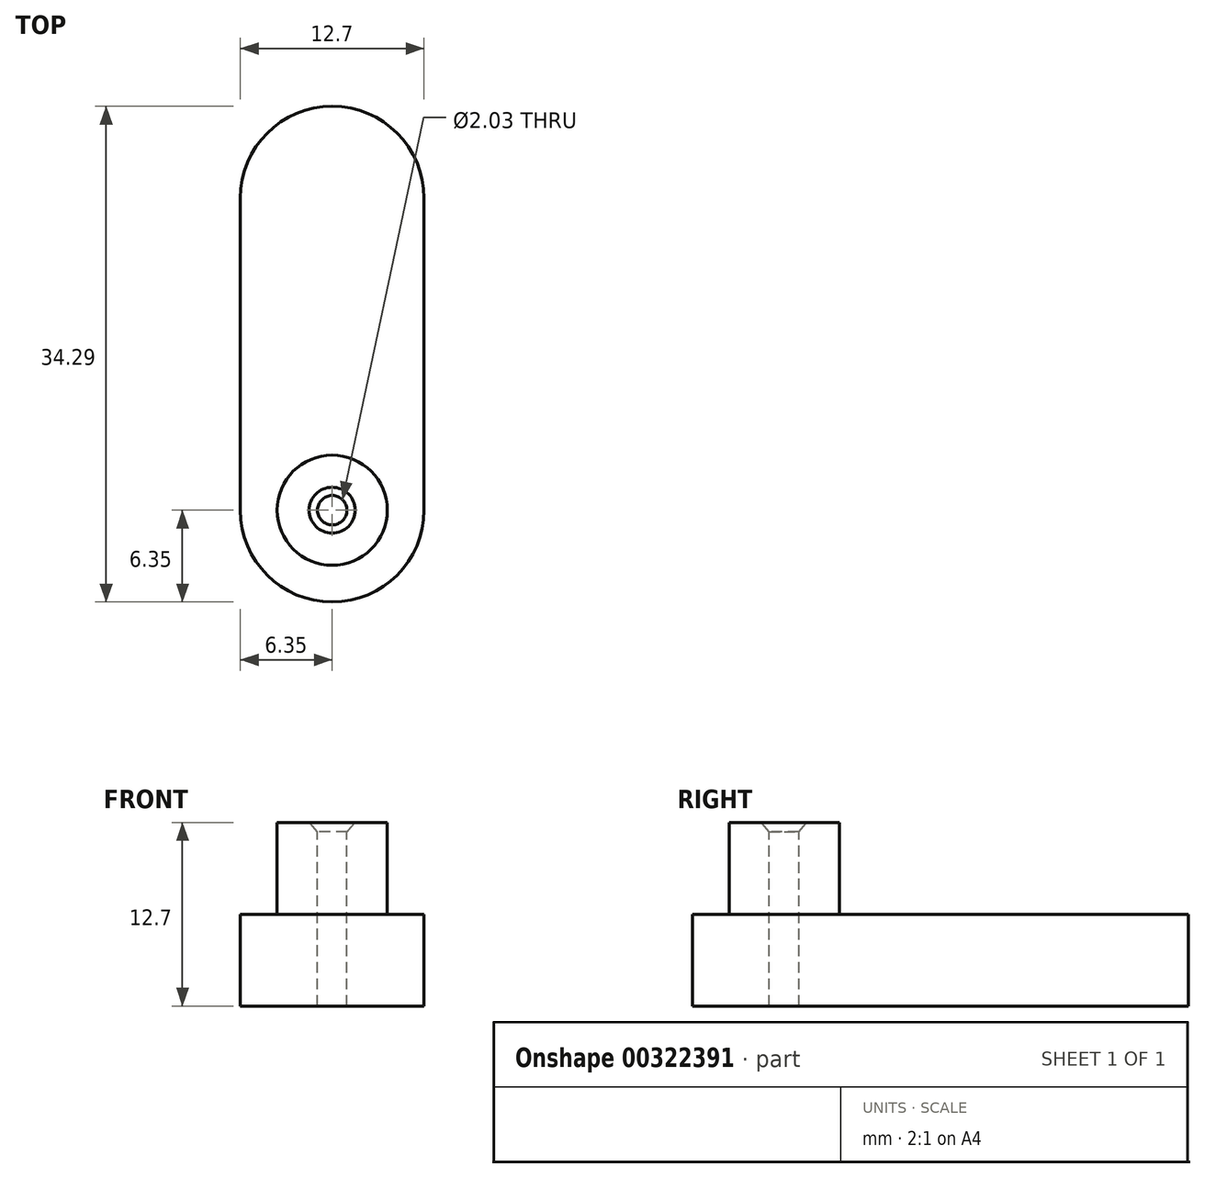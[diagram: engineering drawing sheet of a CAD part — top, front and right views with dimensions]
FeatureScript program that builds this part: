
annotation { "Feature Type Name" : "Feature", "Feature Type Description" : "" }
export const myFeature = defineFeature(function(context is Context, id is Id, definition is map)
    precondition{}
    {
        {
            var Q0;
            Q0=qCreatedBy(makeId("Top.planeOp"),FACE);
            var sketch = newSketch(context, id + "F0", { "sketchPlane" : qUnion([Q0])});
            skLineSegment(sketch, "E0", {"start": v(0, 0) * mm, "end": v(0, 12.7) * mm});
            skLineSegment(sketch, "E1", {"start": v(0, 12.7) * mm, "end": v(0, 34.3) * mm});
            skLineSegment(sketch, "E2", {"start": v(0, 34.3) * mm, "end": v(22.73, 67.98) * mm});
            skArc(sketch, "E3.0.startCap", {"start": v(6.35, 12.7) * mm, "mid": v(0, 6.35) * mm, "end": v(-6.35, 12.7) * mm});
            skArc(sketch, "E3.0.endCap", {"start": v(-6.35, 34.3) * mm, "mid": v(0, 40.64) * mm, "end": v(6.35, 34.3) * mm});
            skLineSegment(sketch, "E3.0.left", {"start": v(-6.35, 12.7) * mm, "end": v(-6.35, 34.3) * mm});
            skLineSegment(sketch, "E3.0.right", {"start": v(6.35, 12.7) * mm, "end": v(6.35, 34.3) * mm});
            skArc(sketch, "E3.1.startCap", {"start": v(6.35, 0) * mm, "mid": v(0, -6.35) * mm, "end": v(-6.35, 0) * mm});
            skArc(sketch, "E3.1.endCap", {"start": v(-6.35, 12.7) * mm, "mid": v(0, 19.05) * mm, "end": v(6.35, 12.7) * mm});
            skLineSegment(sketch, "E3.1.left", {"start": v(-6.35, 0) * mm, "end": v(-6.35, 12.7) * mm});
            skLineSegment(sketch, "E3.1.right", {"start": v(6.35, 0) * mm, "end": v(6.35, 12.7) * mm});
            skArc(sketch, "E3.2.startCap", {"start": v(5.26, 30.74) * mm, "mid": v(-3.55, 29.03) * mm, "end": v(-5.26, 37.84) * mm});
            skArc(sketch, "E3.2.endCap", {"start": v(17.46, 71.53) * mm, "mid": v(26.28, 73.25) * mm, "end": v(27.99, 64.43) * mm});
            skLineSegment(sketch, "E3.2.left", {"start": v(-5.26, 37.84) * mm, "end": v(17.46, 71.53) * mm});
            skLineSegment(sketch, "E3.2.right", {"start": v(5.26, 30.74) * mm, "end": v(27.99, 64.43) * mm});
            skSolve(sketch);
        }
        {
            var Q0;
            Q0=makeQuery(id+"F0.imprint","IMPRINT",FACE,{"disambiguationData":[TD([[makeQuery(id+"F0.imprint","IMPRINT",EDGE,{"derivedFrom":sQuery(id+"F0.wireOp",EDGE,"E3.1.startCap")}),-1.0]])]});
            var Q1;
            {var subQ0=sQuery(id+"F0.wireOp",EDGE,"E3.2.endCap");Q1=makeQuery(id+"F0.imprint","IMPRINT",FACE,{"disambiguationData":[TD([[makeQuery(id+"F0.imprint","IMPRINT",EDGE,{"derivedFrom":subQ0}),-1.0]])]});}
            var Q2;
            {var subQ0=sQuery(id+"F0.wireOp",EDGE,"E1");var subQ1=sQuery(id+"F0.wireOp",EDGE,"E0");var subQ2=makeQuery(id+"F0.imprint","INTERSECT",VERTEX,{"derivedFrom":[subQ1,subQ0]});Q2=makeQuery(id+"F0.imprint","IMPRINT",FACE,{"disambiguationData":[TD([[makeQuery(id+"F0.imprint","IMPRINT",EDGE,{"disambiguationData":[TD([[subQ2,1.0]])],"derivedFrom":subQ1}),-1.0]])]});}
            var Q3;
            {var subQ0=sQuery(id+"F0.wireOp",EDGE,"E1");var subQ1=sQuery(id+"F0.wireOp",EDGE,"E0");var subQ2=makeQuery(id+"F0.imprint","INTERSECT",VERTEX,{"derivedFrom":[subQ1,subQ0]});Q3=makeQuery(id+"F0.imprint","IMPRINT",FACE,{"disambiguationData":[TD([[makeQuery(id+"F0.imprint","IMPRINT",EDGE,{"disambiguationData":[TD([[subQ2,1.0]])],"derivedFrom":subQ1}),1.0]])]});}
            var Q4;
            {var subQ5=sQuery(id+"F0.wireOp",EDGE,"E3.0.left");Q4=makeQuery(id+"F0.imprint","IMPRINT",FACE,{"disambiguationData":[TD([[makeQuery(id+"F0.imprint","IMPRINT",EDGE,{"derivedFrom":subQ5}),-1.0]])]});}
            var Q5;
            {var subQ0=sQuery(id+"F0.wireOp",EDGE,"E3.1.endCap");var subQ3=sQuery(id+"F0.wireOp",EDGE,"E1");var subQ4=makeQuery(id+"F0.imprint","INTERSECT",VERTEX,{"derivedFrom":[subQ3,subQ0]});Q5=makeQuery(id+"F0.imprint","IMPRINT",FACE,{"disambiguationData":[TD([[makeQuery(id+"F0.imprint","IMPRINT",EDGE,{"disambiguationData":[TD([[subQ4,-1.0]])],"derivedFrom":subQ3}),-1.0]])]});}
            var Q6;
            {var subQ3=sQuery(id+"F0.wireOp",EDGE,"E2");var subQ6=sQuery(id+"F0.wireOp",EDGE,"E1");var subQ8=makeQuery(id+"F0.imprint","INTERSECT",VERTEX,{"derivedFrom":[subQ6,subQ3]});Q6=makeQuery(id+"F0.imprint","IMPRINT",FACE,{"disambiguationData":[TD([[makeQuery(id+"F0.imprint","IMPRINT",EDGE,{"disambiguationData":[TD([[subQ8,1.0]])],"derivedFrom":subQ6}),1.0]])]});}
            var Q7;
            {var subQ7=sQuery(id+"F0.wireOp",EDGE,"E2");var subQ8=sQuery(id+"F0.wireOp",EDGE,"E1");var subQ9=makeQuery(id+"F0.imprint","INTERSECT",VERTEX,{"derivedFrom":[subQ8,subQ7]});Q7=makeQuery(id+"F0.imprint","IMPRINT",FACE,{"disambiguationData":[TD([[makeQuery(id+"F0.imprint","IMPRINT",EDGE,{"disambiguationData":[TD([[subQ9,1.0]])],"derivedFrom":subQ8}),-1.0]])]});}
            var Q8;
            Q8 = qConstructionFilter(qBodyType(qCreatedBy(id + "F0" ,EDGE), BodyType.WIRE), ConstructionObject.NO);
            extrude(context, id + "F1", {"entities" : qUnion([Q0, Q1, Q2, Q3, Q4, Q5, Q6, Q7]), "surfaceEntities" : qUnion([Q8]), "depth" : 6.35 * mm});
        }
        {
            var Q0;
            Q0=makeQuery(id+"F1.opExtrude","CAP_FACE",FACE,{"disambiguationData":[OSD([sQuery(id+"F0.wireOp",EDGE,"E3.0.left"),sQuery(id+"F0.wireOp",EDGE,"E3.0.right"),sQuery(id+"F0.wireOp",EDGE,"E3.1.startCap"),sQuery(id+"F0.wireOp",EDGE,"E3.1.left"),sQuery(id+"F0.wireOp",EDGE,"E3.1.right"),sQuery(id+"F0.wireOp",EDGE,"E3.2.startCap"),sQuery(id+"F0.wireOp",EDGE,"E3.2.endCap"),sQuery(id+"F0.wireOp",EDGE,"E3.2.left"),sQuery(id+"F0.wireOp",EDGE,"E3.2.right")])],"isStart":false});
            var sketch = newSketch(context, id + "F2", { "sketchPlane" : qUnion([Q0])});
            skCircle(sketch, "E4", {"center": v(0, 12.7) * mm, "radius": 3.81 * mm});
            skSolve(sketch);
        }
        {
            var Q0;
            Q0 = qSketchRegion(id + "F2", true);
            extrude(context, id + "F3", {"entities" : qUnion([Q0]), "operationType" : NewBodyOperationType.ADD, "depth" : 6.35 * mm});
        }
        {
            var Q0;
            Q0=makeQuery(id+"F3.opExtrude","CAP_FACE",FACE,{"disambiguationData":[OSD([sQuery(id+"F2.wireOp",EDGE,"E4")])],"isStart":false});
            var sketch = newSketch(context, id + "F4", { "sketchPlane" : qUnion([Q0])});
            skPoint(sketch, "E5", {"position": v(0, 12.7) * mm});
            skSolve(sketch);
        }
        {
            var Q0;
            Q0=sQuery(id+"F4.wireOp",VERTEX,"E5");
            var Q1;
            Q1=makeQuery(id+"F1.opExtrude","SWEPT_BODY",BODY,{"disambiguationData":[OSD([sQuery(id+"F0.wireOp",EDGE,"E3.0.left"),sQuery(id+"F0.wireOp",EDGE,"E3.0.right"),sQuery(id+"F0.wireOp",EDGE,"E3.1.startCap"),sQuery(id+"F0.wireOp",EDGE,"E3.1.left"),sQuery(id+"F0.wireOp",EDGE,"E3.1.right"),sQuery(id+"F0.wireOp",EDGE,"E3.2.startCap"),sQuery(id+"F0.wireOp",EDGE,"E3.2.endCap"),sQuery(id+"F0.wireOp",EDGE,"E3.2.left"),sQuery(id+"F0.wireOp",EDGE,"E3.2.right")])]});
            hole(context, id + "F5", {"style" : HoleStyle.C_SINK, "endStyle" : HoleEndStyle.THROUGH, "holeDiameter" : 2.03 * mm, "cSinkDiameter" : 3.17 * mm, "cSinkAngle" : 82 * degree, "tappedDepth" : 12.7 * mm, "tapClearance" : 3, "locations" : qUnion([Q0]), "scope" : qUnion([Q1])});
        }
        {
            var Q0;
            Q0=makeQuery(id+"F1.opExtrude","CAP_FACE",FACE,{"disambiguationData":[OSD([sQuery(id+"F0.wireOp",EDGE,"E3.0.left"),sQuery(id+"F0.wireOp",EDGE,"E3.0.right"),sQuery(id+"F0.wireOp",EDGE,"E3.1.startCap"),sQuery(id+"F0.wireOp",EDGE,"E3.1.left"),sQuery(id+"F0.wireOp",EDGE,"E3.1.right"),sQuery(id+"F0.wireOp",EDGE,"E3.2.startCap"),sQuery(id+"F0.wireOp",EDGE,"E3.2.endCap"),sQuery(id+"F0.wireOp",EDGE,"E3.2.left"),sQuery(id+"F0.wireOp",EDGE,"E3.2.right")])],"isStart":false});
            var sketch = newSketch(context, id + "F6", { "sketchPlane" : qUnion([Q0])});
            skPoint(sketch, "E6", {"position": v(0, 0) * mm});
            skSolve(sketch);
        }
        {
            var Q0;
            Q0=sQuery(id+"F6.wireOp",VERTEX,"E6");
            var Q1;
            Q1=makeQuery(id+"F1.opExtrude","SWEPT_BODY",BODY,{"disambiguationData":[OSD([sQuery(id+"F0.wireOp",EDGE,"E3.0.left"),sQuery(id+"F0.wireOp",EDGE,"E3.0.right"),sQuery(id+"F0.wireOp",EDGE,"E3.1.startCap"),sQuery(id+"F0.wireOp",EDGE,"E3.1.left"),sQuery(id+"F0.wireOp",EDGE,"E3.1.right"),sQuery(id+"F0.wireOp",EDGE,"E3.2.startCap"),sQuery(id+"F0.wireOp",EDGE,"E3.2.endCap"),sQuery(id+"F0.wireOp",EDGE,"E3.2.left"),sQuery(id+"F0.wireOp",EDGE,"E3.2.right")])]});
            hole(context, id + "F7", {"style" : HoleStyle.SIMPLE, "endStyle" : HoleEndStyle.THROUGH, "holeDiameter" : 2.03 * mm, "tappedDepth" : 12.7 * mm, "tapClearance" : 3, "locations" : qUnion([Q0]), "scope" : qUnion([Q1])});
        }
    });
